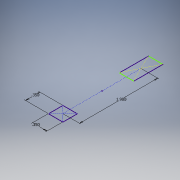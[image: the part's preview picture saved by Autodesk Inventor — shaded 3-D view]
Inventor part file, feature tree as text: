
AUTODESK INVENTOR PART (.ipt)
format: ipt  version: 2016 (Build 200138000, 138)  size: 86,016 bytes
history: native  units: in
note: dims shown in document units (in); Inventor stores cm internally (conversion verified against a paired STEP export)
features: sketch x1
ambient origin geometry x8: Origin, YZ Plane, XZ Plane, XY Plane, X Axis, Y Axis, Z Axis, Center Point
feature tree (1):
  sketch  "Sketch1"  dims[d0=1.9in d1=0.35in d2=0.35in]
